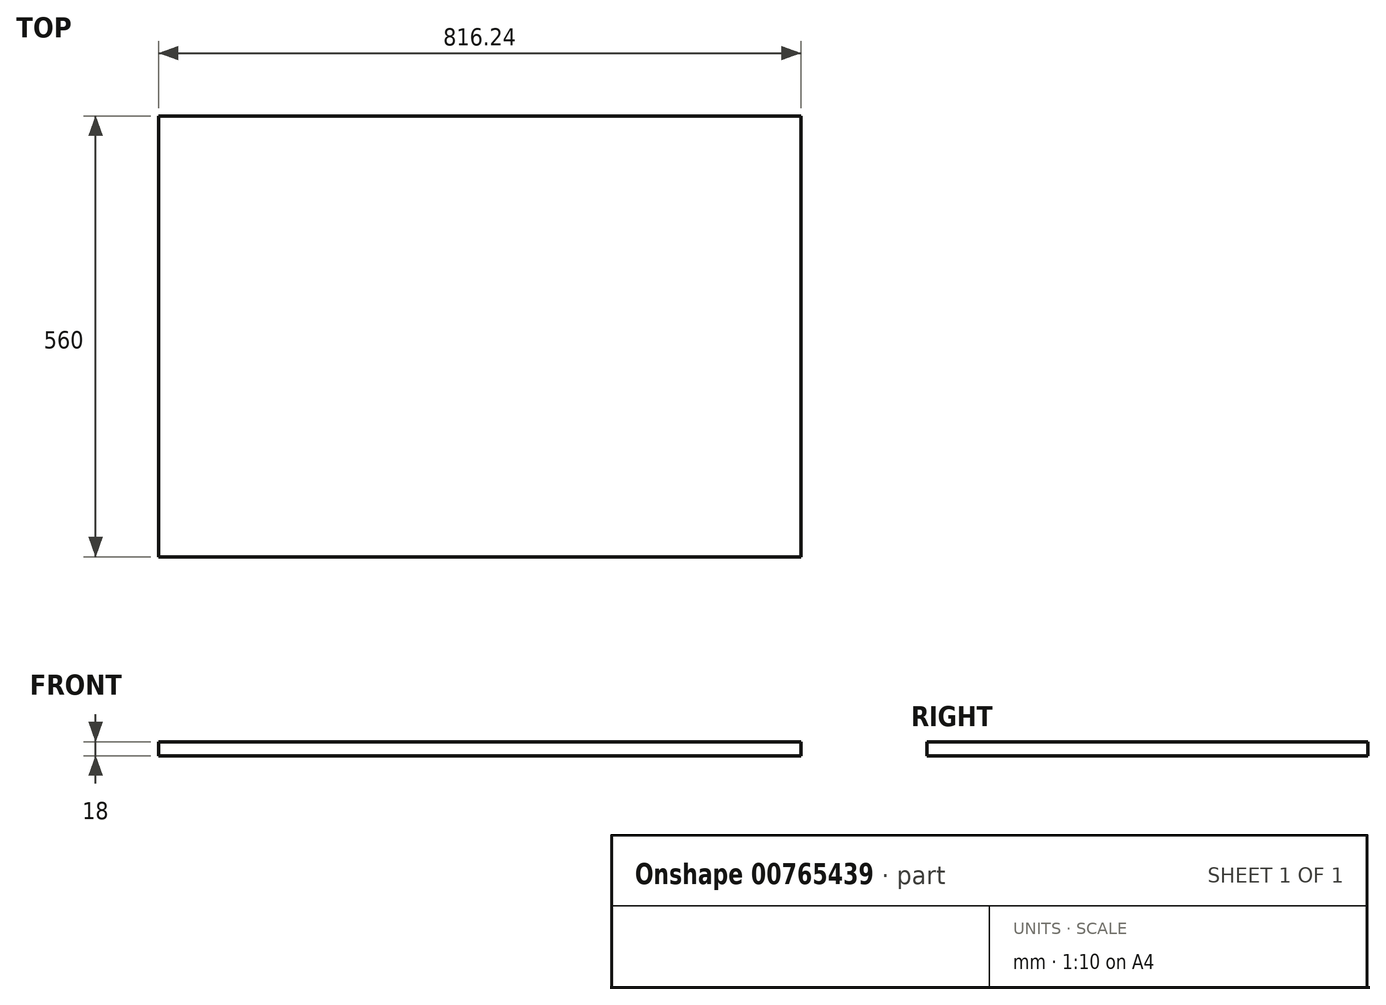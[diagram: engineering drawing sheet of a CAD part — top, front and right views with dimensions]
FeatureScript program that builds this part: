
annotation { "Feature Type Name" : "Feature", "Feature Type Description" : "" }
export const myFeature = defineFeature(function(context is Context, id is Id, definition is map)
    precondition{}
    {
        {
            var Q0;
            Q0=qCreatedBy(makeId("Top.planeOp"),FACE);
            var sketch = newSketch(context, id + "F0", { "sketchPlane" : qUnion([Q0])});
            skLineSegment(sketch, "E0.bottom", {"start": v(-408.13, -280) * mm, "end": v(408.13, -280) * mm});
            skLineSegment(sketch, "E0.top", {"start": v(-408.13, 280) * mm, "end": v(408.12, 280) * mm});
            skLineSegment(sketch, "E0.left", {"start": v(-408.13, -280) * mm, "end": v(-408.13, 280) * mm});
            skLineSegment(sketch, "E0.right", {"start": v(408.13, -280) * mm, "end": v(408.12, 280) * mm});
            skPoint(sketch, "E0.middle", {"position": v(0, 0) * mm});
            skSolve(sketch);
        }
        {
            var Q0;
            Q0 = qSketchRegion(id + "F0", true);
            extrude(context, id + "F1", {"entities" : qUnion([Q0]), "depth" : 18 * mm, "offsetDistance" : 25 * mm});
        }
    });
